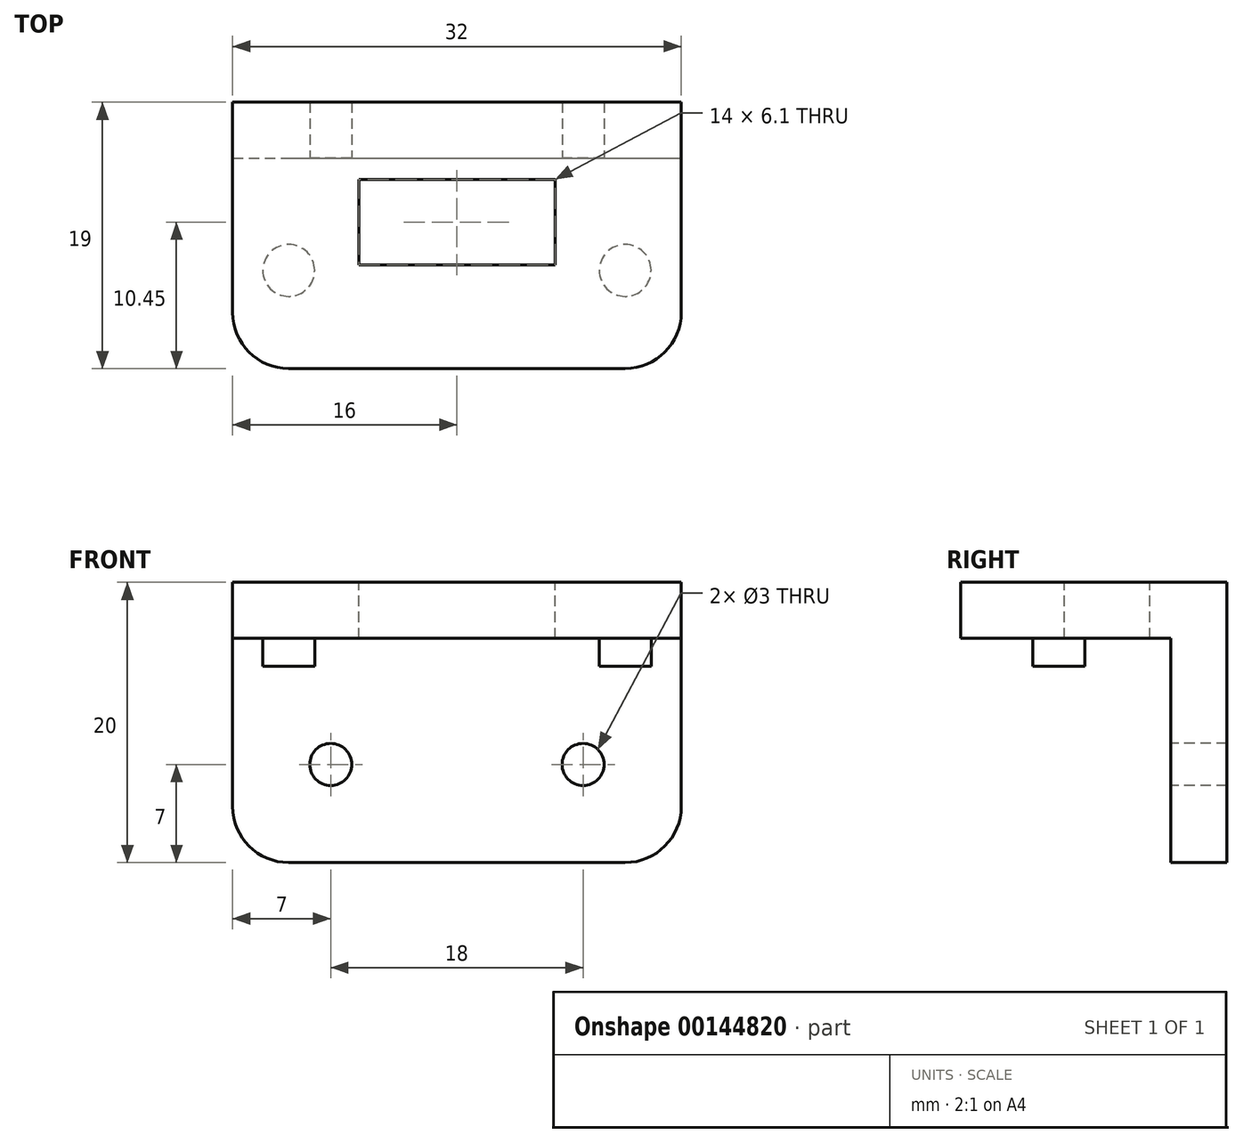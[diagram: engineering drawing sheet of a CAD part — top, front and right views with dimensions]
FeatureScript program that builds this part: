
annotation { "Feature Type Name" : "Feature", "Feature Type Description" : "" }
export const myFeature = defineFeature(function(context is Context, id is Id, definition is map)
    precondition{}
    {
        {
            var Q0;
            Q0=qCreatedBy(makeId("Top.planeOp"),FACE);
            var sketch = newSketch(context, id + "F0", { "sketchPlane" : qUnion([Q0])});
            skLineSegment(sketch, "E0.bottom", {"start": v(-16, 9.5) * mm, "end": v(16, 9.5) * mm});
            skLineSegment(sketch, "E0.top", {"start": v(-16, -9.5) * mm, "end": v(16, -9.5) * mm});
            skLineSegment(sketch, "E0.left", {"start": v(-16, 9.5) * mm, "end": v(-16, -9.5) * mm});
            skLineSegment(sketch, "E0.right", {"start": v(16, 9.5) * mm, "end": v(16, -9.5) * mm});
            skPoint(sketch, "E0.middle", {"position": v(0, 0) * mm});
            skSolve(sketch);
        }
        {
            var Q0;
            Q0 = qSketchRegion(id + "F0", true);
            var Q1;
            Q1=makeQuery(id+"F0.imprint","IMPRINT",FACE,{"disambiguationData":[TD([[makeQuery(id+"F0.imprint","IMPRINT",EDGE,{"derivedFrom":sQuery(id+"F0.wireOp",EDGE,"E0.bottom")}),-1.0]])]});
            extrude(context, id + "F1", {"entities" : qUnion([Q0, Q1]), "depth" : 4 * mm});
        }
        {
            var Q0;
            Q0=makeQuery(id+"F1.opExtrude","CAP_FACE",FACE,{"disambiguationData":[OSD([sQuery(id+"F0.wireOp",EDGE,"E0.bottom"),sQuery(id+"F0.wireOp",EDGE,"E0.top"),sQuery(id+"F0.wireOp",EDGE,"E0.left"),sQuery(id+"F0.wireOp",EDGE,"E0.right")])],"isStart":true});
            var sketch = newSketch(context, id + "F2", { "sketchPlane" : qUnion([Q0])});
            skLineSegment(sketch, "E1.bottom", {"start": v(-16, -9.5) * mm, "end": v(16, -9.5) * mm});
            skLineSegment(sketch, "E1.top", {"start": v(-16, -5.5) * mm, "end": v(16, -5.5) * mm});
            skLineSegment(sketch, "E1.left", {"start": v(-16, -9.5) * mm, "end": v(-16, -5.5) * mm});
            skLineSegment(sketch, "E1.right", {"start": v(16, -9.5) * mm, "end": v(16, -5.5) * mm});
            skSolve(sketch);
        }
        {
            var Q0;
            Q0 = qSketchRegion(id + "F2", true);
            extrude(context, id + "F3", {"entities" : qUnion([Q0]), "operationType" : NewBodyOperationType.ADD, "depth" : 16 * mm});
        }
        {
            var Q0;
            Q0=makeQuery(id+"F3.opExtrude","SWEPT_FACE",FACE,{"disambiguationData":[OSD([sQuery(id+"F2.wireOp",EDGE,"E1.top")])]});
            var sketch = newSketch(context, id + "F4", { "sketchPlane" : qUnion([Q0])});
            skPoint(sketch, "E2", {"position": v(9, -9) * mm});
            skPoint(sketch, "E3.MirrorP", {"position": v(-9, -9) * mm});
            skSolve(sketch);
        }
        {
            var Q0;
            Q0=makeQuery(id+"F1.opExtrude","CAP_FACE",FACE,{"disambiguationData":[OSD([sQuery(id+"F0.wireOp",EDGE,"E0.bottom"),sQuery(id+"F0.wireOp",EDGE,"E0.top"),sQuery(id+"F0.wireOp",EDGE,"E0.left"),sQuery(id+"F0.wireOp",EDGE,"E0.right")])],"isStart":false});
            var sketch = newSketch(context, id + "F5", { "sketchPlane" : qUnion([Q0])});
            skLineSegment(sketch, "E4.bottom", {"start": v(-7, -2.1) * mm, "end": v(7, -2.1) * mm});
            skLineSegment(sketch, "E4.top", {"start": v(-7, 4) * mm, "end": v(7, 4) * mm});
            skLineSegment(sketch, "E4.left", {"start": v(-7, -2.1) * mm, "end": v(-7, 4) * mm});
            skLineSegment(sketch, "E4.right", {"start": v(7, -2.1) * mm, "end": v(7, 4) * mm});
            skPoint(sketch, "E4.middle", {"position": v(0, 0.95) * mm});
            skSolve(sketch);
        }
        {
            var Q0;
            Q0=makeQuery(id+"F5.imprint","IMPRINT",FACE,{"disambiguationData":[TD([[makeQuery(id+"F5.imprint","IMPRINT",EDGE,{"derivedFrom":sQuery(id+"F5.wireOp",EDGE,"E4.bottom")}),1.0]])]});
            extrude(context, id + "F6", {"entities" : qUnion([Q0]), "operationType" : NewBodyOperationType.REMOVE, "oppositeDirection" : true, "depth" : 25 * mm});
        }
        {
            var Q0;
            Q0=makeQuery(id+"F1.opExtrude","CAP_FACE",FACE,{"disambiguationData":[OSD([sQuery(id+"F0.wireOp",EDGE,"E0.bottom"),sQuery(id+"F0.wireOp",EDGE,"E0.top"),sQuery(id+"F0.wireOp",EDGE,"E0.left"),sQuery(id+"F0.wireOp",EDGE,"E0.right")])],"isStart":true});
            var sketch = newSketch(context, id + "F7", { "sketchPlane" : qUnion([Q0])});
            skPoint(sketch, "E5", {"position": v(-12, 2.5) * mm});
            skCircle(sketch, "E6", {"center": v(-12, 2.5) * mm, "radius": 1.85 * mm});
            skCircle(sketch, "E7.MirrorC", {"center": v(12, 2.5) * mm, "radius": 1.85 * mm});
            skSolve(sketch);
        }
        {
            var Q0;
            Q0 = qSketchRegion(id + "F7", true);
            extrude(context, id + "F8", {"entities" : qUnion([Q0]), "operationType" : NewBodyOperationType.ADD, "depth" : 2 * mm});
        }
        {
            var Q0;
            Q0=sQuery(id+"F4.wireOp",VERTEX,"E3.MirrorP");
            var Q1;
            Q1=sQuery(id+"F4.wireOp",VERTEX,"E2");
            var Q2;
            Q2=makeQuery(id+"F1.opExtrude","SWEPT_BODY",BODY,{"disambiguationData":[OSD([sQuery(id+"F0.wireOp",EDGE,"E0.bottom"),sQuery(id+"F0.wireOp",EDGE,"E0.top"),sQuery(id+"F0.wireOp",EDGE,"E0.left"),sQuery(id+"F0.wireOp",EDGE,"E0.right")])]});
            hole(context, id + "F9", {"style" : HoleStyle.SIMPLE, "endStyle" : HoleEndStyle.THROUGH, "holeDiameter" : 3 * mm, "locations" : qUnion([Q0, Q1]), "scope" : qUnion([Q2]), "isTappedThrough" : true});
        }
        {
            var Q0;
            Q0=makeQuery(id+"F1.opExtrude","SWEPT_EDGE",EDGE,{"disambiguationData":[OSD([sQuery(id+"F0.wireOp",EDGE,"E0.top"),sQuery(id+"F0.wireOp",EDGE,"E0.right")])]});
            var Q1;
            Q1=makeQuery(id+"F1.opExtrude","SWEPT_EDGE",EDGE,{"disambiguationData":[OSD([sQuery(id+"F0.wireOp",EDGE,"E0.top"),sQuery(id+"F0.wireOp",EDGE,"E0.left")])]});
            var Q2;
            Q2=makeQuery(id+"F3.opExtrude","CAP_EDGE",EDGE,{"disambiguationData":[OSD([sQuery(id+"F2.wireOp",EDGE,"E1.left")])],"isStart":false});
            var Q3;
            Q3=makeQuery(id+"F3.opExtrude","CAP_EDGE",EDGE,{"disambiguationData":[OSD([sQuery(id+"F2.wireOp",EDGE,"E1.right")])],"isStart":false});
            fillet(context, id + "F10", {"entities" : qUnion([Q0, Q1, Q2, Q3]), "radius" : 4 * mm, "tangentPropagation" : true, "allowEdgeOverflow" : false});
        }
    });
